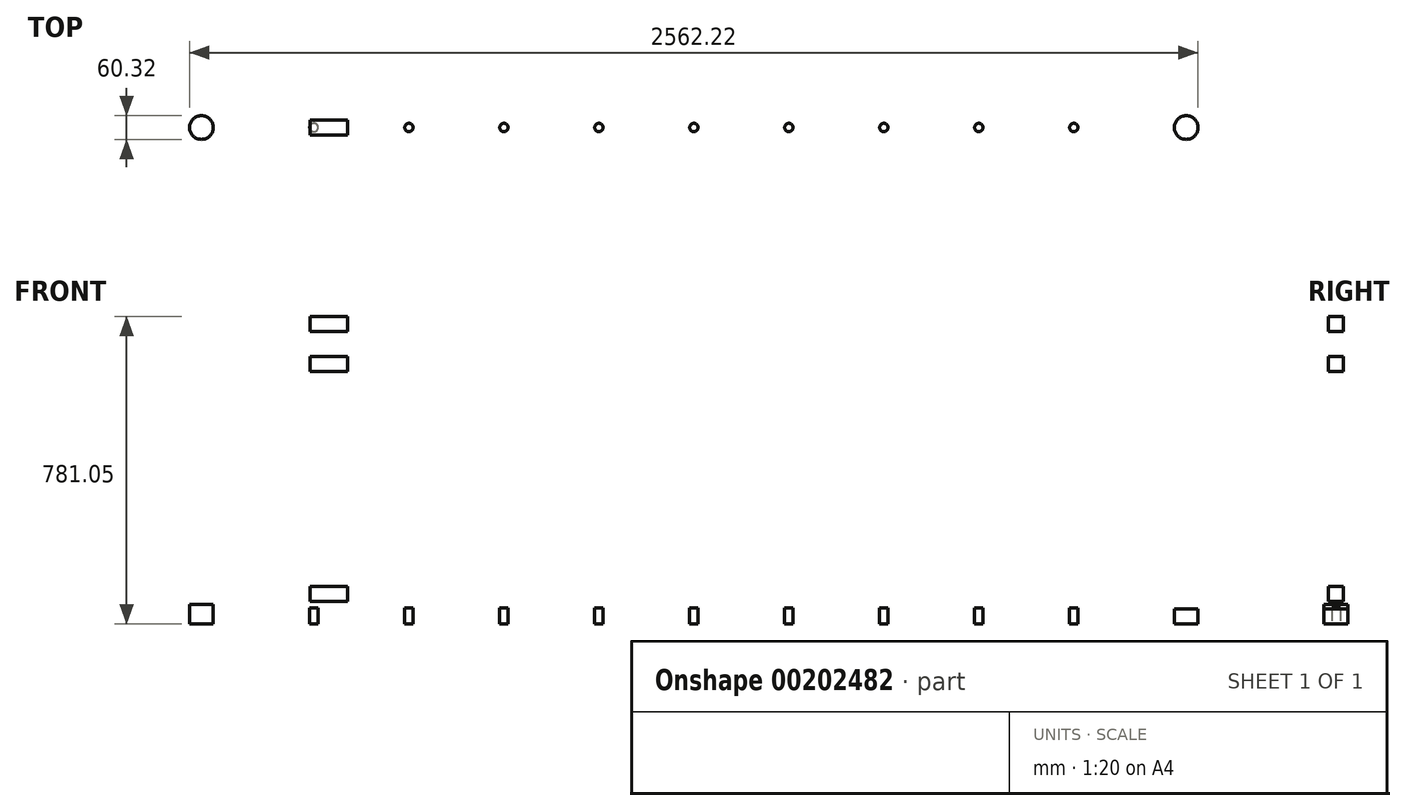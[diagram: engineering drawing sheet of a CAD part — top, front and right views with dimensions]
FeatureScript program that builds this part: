
annotation { "Feature Type Name" : "Feature", "Feature Type Description" : "" }
export const myFeature = defineFeature(function(context is Context, id is Id, definition is map)
    precondition{}
    {
        {
            assignVariable(context, id + "F0", {"name" : "BarLength", "anyValue" : 96});
        }
        {
            assignVariable(context, id + "F1", {"name" : "SpacingEnds", "anyValue" : 10});
        }
        {
            assignVariable(context, id + "F2", {"name" : "HeightTall", "anyValue" : 40});
        }
        {
            assignVariable(context, id + "F3", {"name" : "HeightMedium", "anyValue" : 40});
        }
        {
            assignVariable(context, id + "F4", {"name" : "HeightShort", "anyValue" : 40});
        }
        {
            assignVariable(context, id + "F5", {"name" : "HeightCorner", "anyValue" : 50});
        }
        {
            assignVariable(context, id + "F6", {"name" : "HeightPost", "anyValue" : getVariable(context, 'HeightTall') - 2});
        }
        {
            var Q0;
            Q0=qCreatedBy(makeId("Top.planeOp"),FACE);
            var sketch = newSketch(context, id + "F7", { "sketchPlane" : qUnion([Q0])});
            skCircle(sketch, "E0", {"center": v(0, 0) * mm, "radius": 10.67 * mm});
            skCircle(sketch, "E1.1.0.0", {"center": v(241.3, 0) * mm, "radius": 10.67 * mm});
            skCircle(sketch, "E1.2.0.0", {"center": v(482.6, 0) * mm, "radius": 10.67 * mm});
            skCircle(sketch, "E1.3.0.0", {"center": v(723.9, 0) * mm, "radius": 10.67 * mm});
            skCircle(sketch, "E1.4.0.0", {"center": v(965.2, 0) * mm, "radius": 10.67 * mm});
            skLineSegment(sketch, "E1.direction1", {"start": v(0, 0) * mm, "end": v(241.3, 0) * mm, "construction": true});
            skCircle(sketch, "E2", {"center": v(2216.15, 0) * mm, "radius": 30.16 * mm});
            skCircle(sketch, "E3.0.5.0", {"center": v(1206.5, 0) * mm, "radius": 10.67 * mm});
            skCircle(sketch, "E3.0.6.0", {"center": v(1447.8, 0) * mm, "radius": 10.67 * mm});
            skCircle(sketch, "E3.0.7.0", {"center": v(1689.1, 0) * mm, "radius": 10.67 * mm});
            skCircle(sketch, "E3.0.8.0", {"center": v(1930.4, 0) * mm, "radius": 10.67 * mm});
            skCircle(sketch, "E4", {"center": v(-285.75, 0) * mm, "radius": 30.16 * mm});
            skSolve(sketch);
        }
        {
            var Q0;
            Q0=qCreatedBy(makeId("Right.planeOp"),FACE);
            var sketch = newSketch(context, id + "F8", { "sketchPlane" : qUnion([Q0])});
            skLineSegment(sketch, "E5.bottom", {"start": v(19.05, 95.25) * mm, "end": v(-19.05, 95.25) * mm});
            skLineSegment(sketch, "E5.top", {"start": v(19.05, 57.15) * mm, "end": v(-19.05, 57.15) * mm});
            skLineSegment(sketch, "E5.left", {"start": v(19.05, 95.25) * mm, "end": v(19.05, 57.15) * mm});
            skLineSegment(sketch, "E5.right", {"start": v(-19.05, 95.25) * mm, "end": v(-19.05, 57.15) * mm});
            skPoint(sketch, "E5.middle", {"position": v(0, 76.2) * mm});
            skLineSegment(sketch, "E6.bottom", {"start": v(19.05, 641.35) * mm, "end": v(-19.05, 641.35) * mm});
            skLineSegment(sketch, "E6.top", {"start": v(19.05, 679.45) * mm, "end": v(-19.05, 679.45) * mm});
            skLineSegment(sketch, "E6.left", {"start": v(19.05, 641.35) * mm, "end": v(19.05, 679.45) * mm});
            skLineSegment(sketch, "E6.right", {"start": v(-19.05, 641.35) * mm, "end": v(-19.05, 679.45) * mm});
            skPoint(sketch, "E6.middle", {"position": v(0, 660.4) * mm});
            skLineSegment(sketch, "E7.bottom", {"start": v(19.05, 742.95) * mm, "end": v(-19.05, 742.95) * mm});
            skLineSegment(sketch, "E7.top", {"start": v(19.05, 781.05) * mm, "end": v(-19.05, 781.05) * mm});
            skLineSegment(sketch, "E7.left", {"start": v(19.05, 742.95) * mm, "end": v(19.05, 781.05) * mm});
            skLineSegment(sketch, "E7.right", {"start": v(-19.05, 742.95) * mm, "end": v(-19.05, 781.05) * mm});
            skPoint(sketch, "E7.middle", {"position": v(0, 762) * mm});
            skSolve(sketch);
        }
        {
            var Q0;
            Q0=makeQuery(id+"F7.imprint","IMPRINT",FACE,{"disambiguationData":[TD([[makeQuery(id+"F7.imprint","IMPRINT",EDGE,{"derivedFrom":sQuery(id+"F7.wireOp",EDGE,"3eb81b25-2982-4639-aaac-831597b73f070.MirrorC")}),-1.0]])]});
            var Q1;
            Q1=makeQuery(id+"F7.imprint","IMPRINT",FACE,{"disambiguationData":[TD([[makeQuery(id+"F7.imprint","IMPRINT",EDGE,{"derivedFrom":sQuery(id+"F7.wireOp",EDGE,"E0")}),1.0]])]});
            var Q2;
            Q2=makeQuery(id+"F7.imprint","IMPRINT",FACE,{"disambiguationData":[TD([[makeQuery(id+"F7.imprint","IMPRINT",EDGE,{"derivedFrom":sQuery(id+"F7.wireOp",EDGE,"E1.4.0.0")}),1.0]])]});
            var Q3;
            Q3=makeQuery(id+"F7.imprint","IMPRINT",FACE,{"disambiguationData":[TD([[makeQuery(id+"F7.imprint","IMPRINT",EDGE,{"derivedFrom":sQuery(id+"F7.wireOp",EDGE,"E3.0.8.0")}),1.0]])]});
            var Q4;
            Q4=sQuery(id+"F7.wireOp",EDGE,"3eb81b25-2982-4639-aaac-831597b73f070.MirrorC");
            var Q5;
            Q5=sQuery(id+"F7.wireOp",EDGE,"E0");
            var Q6;
            Q6=sQuery(id+"F7.wireOp",EDGE,"E1.4.0.0");
            extrude(context, id + "F9", {"entities" : qUnion([Q0, Q1, Q2, Q3]), "surfaceEntities" : qUnion([Q4, Q5, Q6]), "depth" : (getVariable(context, 'HeightShort')) * mm});
        }
        {
            var Q0;
            Q0=makeQuery(id+"F7.imprint","IMPRINT",FACE,{"disambiguationData":[TD([[makeQuery(id+"F7.imprint","IMPRINT",EDGE,{"derivedFrom":sQuery(id+"F7.wireOp",EDGE,"3eb81b25-2982-4639-aaac-831597b73f072.MirrorC")}),-1.0]])]});
            var Q1;
            Q1=makeQuery(id+"F7.imprint","IMPRINT",FACE,{"disambiguationData":[TD([[makeQuery(id+"F7.imprint","IMPRINT",EDGE,{"derivedFrom":sQuery(id+"F7.wireOp",EDGE,"3eb81b25-2982-4639-aaac-831597b73f073.MirrorC")}),-1.0]])]});
            var Q2;
            Q2=makeQuery(id+"F7.imprint","IMPRINT",FACE,{"disambiguationData":[TD([[makeQuery(id+"F7.imprint","IMPRINT",EDGE,{"derivedFrom":sQuery(id+"F7.wireOp",EDGE,"E1.1.0.0")}),1.0]])]});
            var Q3;
            Q3=makeQuery(id+"F7.imprint","IMPRINT",FACE,{"disambiguationData":[TD([[makeQuery(id+"F7.imprint","IMPRINT",EDGE,{"derivedFrom":sQuery(id+"F7.wireOp",EDGE,"E1.3.0.0")}),1.0]])]});
            var Q4;
            Q4=makeQuery(id+"F7.imprint","IMPRINT",FACE,{"disambiguationData":[TD([[makeQuery(id+"F7.imprint","IMPRINT",EDGE,{"derivedFrom":sQuery(id+"F7.wireOp",EDGE,"E3.0.5.0")}),1.0]])]});
            var Q5;
            Q5=makeQuery(id+"F7.imprint","IMPRINT",FACE,{"disambiguationData":[TD([[makeQuery(id+"F7.imprint","IMPRINT",EDGE,{"derivedFrom":sQuery(id+"F7.wireOp",EDGE,"E3.0.7.0")}),1.0]])]});
            extrude(context, id + "F10", {"entities" : qUnion([Q0, Q1, Q2, Q3, Q4, Q5]), "depth" : (getVariable(context, 'HeightMedium')) * mm});
        }
        {
            var Q0;
            Q0=makeQuery(id+"F7.imprint","IMPRINT",FACE,{"disambiguationData":[TD([[makeQuery(id+"F7.imprint","IMPRINT",EDGE,{"derivedFrom":sQuery(id+"F7.wireOp",EDGE,"3eb81b25-2982-4639-aaac-831597b73f071.MirrorC")}),-1.0]])]});
            var Q1;
            Q1=makeQuery(id+"F7.imprint","IMPRINT",FACE,{"disambiguationData":[TD([[makeQuery(id+"F7.imprint","IMPRINT",EDGE,{"derivedFrom":sQuery(id+"F7.wireOp",EDGE,"E1.2.0.0")}),1.0]])]});
            var Q2;
            Q2=makeQuery(id+"F7.imprint","IMPRINT",FACE,{"disambiguationData":[TD([[makeQuery(id+"F7.imprint","IMPRINT",EDGE,{"derivedFrom":sQuery(id+"F7.wireOp",EDGE,"E3.0.6.0")}),1.0]])]});
            extrude(context, id + "F11", {"entities" : qUnion([Q0, Q1, Q2]), "depth" : (getVariable(context, 'HeightTall')) * mm});
        }
        {
            var Q0;
            Q0=makeQuery(id+"F8.imprint","IMPRINT",FACE,{"disambiguationData":[TD([[makeQuery(id+"F8.imprint","IMPRINT",EDGE,{"derivedFrom":sQuery(id+"F8.wireOp",EDGE,"E7.bottom")}),-1.0]])]});
            var Q1;
            Q1=makeQuery(id+"F8.imprint","IMPRINT",FACE,{"disambiguationData":[TD([[makeQuery(id+"F8.imprint","IMPRINT",EDGE,{"derivedFrom":sQuery(id+"F8.wireOp",EDGE,"E6.bottom")}),-1.0]])]});
            var Q2;
            Q2=makeQuery(id+"F8.imprint","IMPRINT",FACE,{"disambiguationData":[TD([[makeQuery(id+"F8.imprint","IMPRINT",EDGE,{"derivedFrom":sQuery(id+"F8.wireOp",EDGE,"E5.bottom")}),1.0]])]});
            extrude(context, id + "F12", {"entities" : qUnion([Q0, Q1, Q2]), "operationType" : NewBodyOperationType.ADD, "depth" : (getVariable(context, 'BarLength') - getVariable(context, 'SpacingEnds')) * mm, "hasSecondDirection" : true, "secondDirectionOppositeDirection" : true, "secondDirectionDepth" : (getVariable(context, 'SpacingEnds')) * mm});
        }
        {
            var Q0;
            Q0=makeQuery(id+"F7.imprint","IMPRINT",FACE,{"disambiguationData":[TD([[makeQuery(id+"F7.imprint","IMPRINT",EDGE,{"derivedFrom":sQuery(id+"F7.wireOp",EDGE,"E4")}),1.0]])]});
            extrude(context, id + "F13", {"entities" : qUnion([Q0]), "depth" : (getVariable(context, 'HeightCorner')) * mm});
        }
        {
            var Q0;
            Q0=makeQuery(id+"F7.imprint","IMPRINT",FACE,{"disambiguationData":[TD([[makeQuery(id+"F7.imprint","IMPRINT",EDGE,{"derivedFrom":sQuery(id+"F7.wireOp",EDGE,"E2")}),1.0]])]});
            extrude(context, id + "F14", {"entities" : qUnion([Q0]), "depth" : (getVariable(context, 'HeightPost')) * mm});
        }
    });
